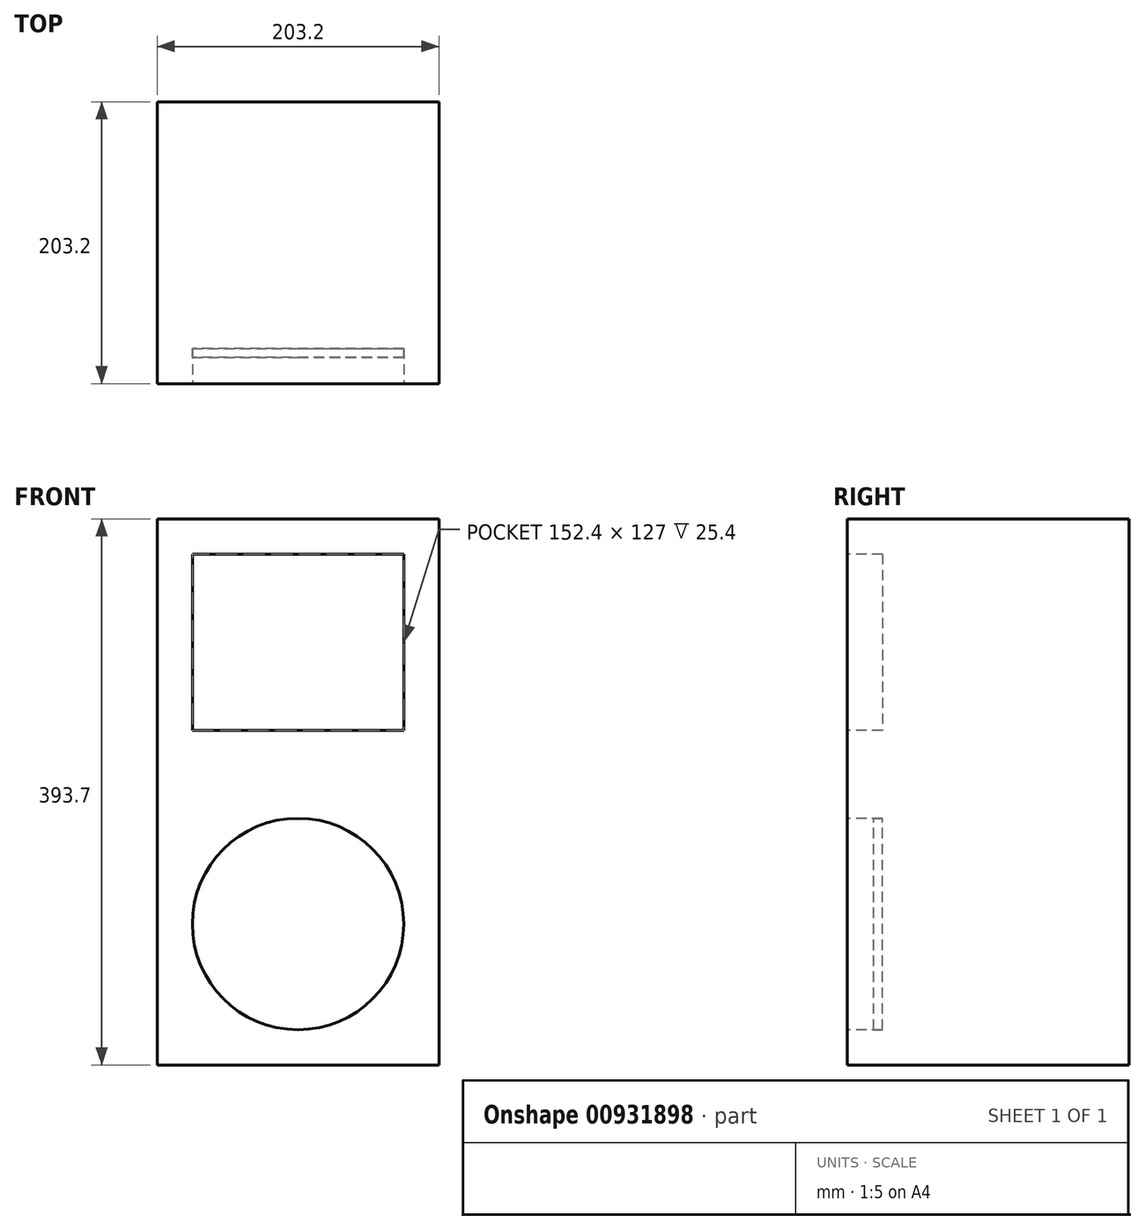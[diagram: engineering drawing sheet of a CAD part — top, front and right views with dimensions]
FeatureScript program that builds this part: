
annotation { "Feature Type Name" : "Feature", "Feature Type Description" : "" }
export const myFeature = defineFeature(function(context is Context, id is Id, definition is map)
    precondition{}
    {
        {
            var Q0;
            Q0=qCreatedBy(makeId("Front.planeOp"),FACE);
            var sketch = newSketch(context, id + "F0", { "sketchPlane" : qUnion([Q0])});
            skLineSegment(sketch, "E0.bottom", {"start": v(0, 0) * mm, "end": v(203.2, 0) * mm});
            skLineSegment(sketch, "E0.top", {"start": v(0, -393.7) * mm, "end": v(203.2, -393.7) * mm});
            skLineSegment(sketch, "E0.left", {"start": v(0, 0) * mm, "end": v(0, -393.7) * mm});
            skLineSegment(sketch, "E0.right", {"start": v(203.2, 0) * mm, "end": v(203.2, -393.7) * mm});
            skSolve(sketch);
        }
        {
            var Q0;
            Q0 = qSketchRegion(id + "F0", true);
            extrude(context, id + "F1", {"entities" : qUnion([Q0]), "oppositeDirection" : true, "depth" : 203.2 * mm, "offsetDistance" : 25.4 * mm});
        }
        {
            var Q0;
            Q0=makeQuery(id+"F1.opExtrude","CAP_FACE",FACE,{"disambiguationData":[OSD([sQuery(id+"F0.wireOp",EDGE,"E0.bottom"),sQuery(id+"F0.wireOp",EDGE,"E0.top"),sQuery(id+"F0.wireOp",EDGE,"E0.left"),sQuery(id+"F0.wireOp",EDGE,"E0.right")])],"isStart":true});
            var sketch = newSketch(context, id + "F2", { "sketchPlane" : qUnion([Q0])});
            skCircle(sketch, "E1", {"center": v(101.6, -292.1) * mm, "radius": 76.2 * mm});
            skLineSegment(sketch, "E2.bottom", {"start": v(25.4, -25.4) * mm, "end": v(177.8, -25.4) * mm});
            skLineSegment(sketch, "E2.top", {"start": v(25.4, -152.4) * mm, "end": v(177.8, -152.4) * mm});
            skLineSegment(sketch, "E2.left", {"start": v(25.4, -25.4) * mm, "end": v(25.4, -152.4) * mm});
            skLineSegment(sketch, "E2.right", {"start": v(177.8, -25.4) * mm, "end": v(177.8, -152.4) * mm});
            skSolve(sketch);
        }
        {
            var Q0;
            Q0 = qSketchRegion(id + "F2", true);
            extrude(context, id + "F3", {"entities" : qUnion([Q0]), "operationType" : NewBodyOperationType.REMOVE, "oppositeDirection" : true, "depth" : 25.4 * mm, "offsetDistance" : 25.4 * mm});
        }
        {
            var Q0;
            Q0=makeQuery(id+"F3.boolean.opBoolean","COPY",FACE,{"derivedFrom":makeQuery(id+"F3.opExtrude","CAP_FACE",FACE,{"disambiguationData":[OSD([sQuery(id+"F2.wireOp",EDGE,"E1")])],"isStart":false})});
            extrude(context, id + "F4", {"entities" : qUnion([Q0]), "depth" : 6.35 * mm, "offsetDistance" : 25.4 * mm});
        }
    });
